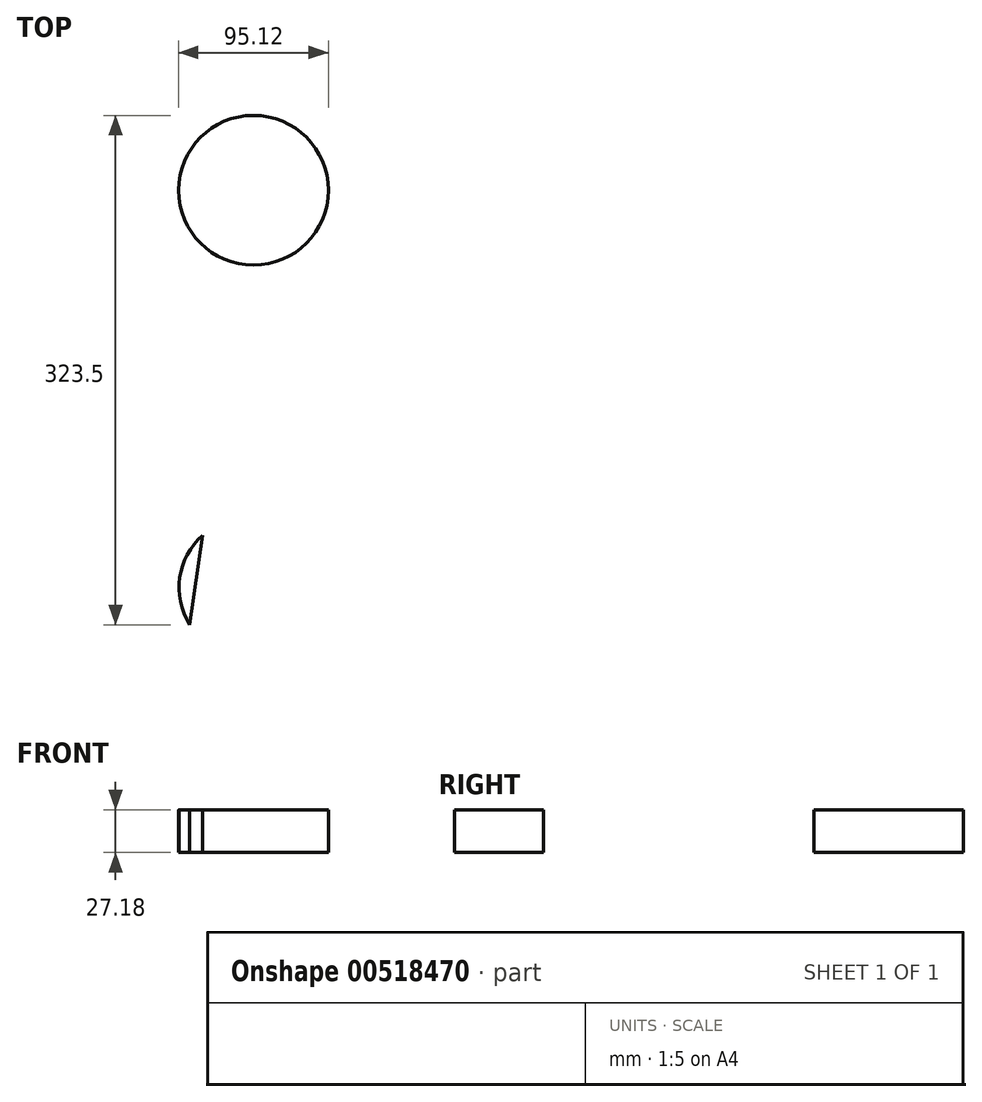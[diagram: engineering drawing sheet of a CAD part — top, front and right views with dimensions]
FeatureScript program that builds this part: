
annotation { "Feature Type Name" : "Feature", "Feature Type Description" : "" }
export const myFeature = defineFeature(function(context is Context, id is Id, definition is map)
    precondition{}
    {
        {
            var Q0;
            Q0=qCreatedBy(makeId("Top.planeOp"),FACE);
            var sketch = newSketch(context, id + "F0", { "sketchPlane" : qUnion([Q0])});
            skLineSegment(sketch, "E0", {"start": v(-28.15, -78.43) * mm, "end": v(-17.36, 85.35) * mm});
            skLineSegment(sketch, "E1", {"start": v(0, -123.56) * mm, "end": v(11.86, 14.77) * mm});
            skArc(sketch, "E2", {"start": v(0, -123.56) * mm, "mid": v(-81.8, -143.24) * mm, "end": v(-28.15, -78.43) * mm});
            skLineSegment(sketch, "E3", {"start": v(-81.8, -143.24) * mm, "end": v(-41.24, 132.7) * mm});
            skCircle(sketch, "E4", {"center": v(-41.24, 132.7) * mm, "radius": 47.56 * mm});
            skSolve(sketch);
        }
        {
            var Q0;
            Q0 = qSketchRegion(id + "F0", true);
            extrude(context, id + "F1", {"entities" : qUnion([Q0]), "oppositeDirection" : true, "depth" : 27.18 * mm, "offsetDistance" : 25.4 * mm});
        }
    });
